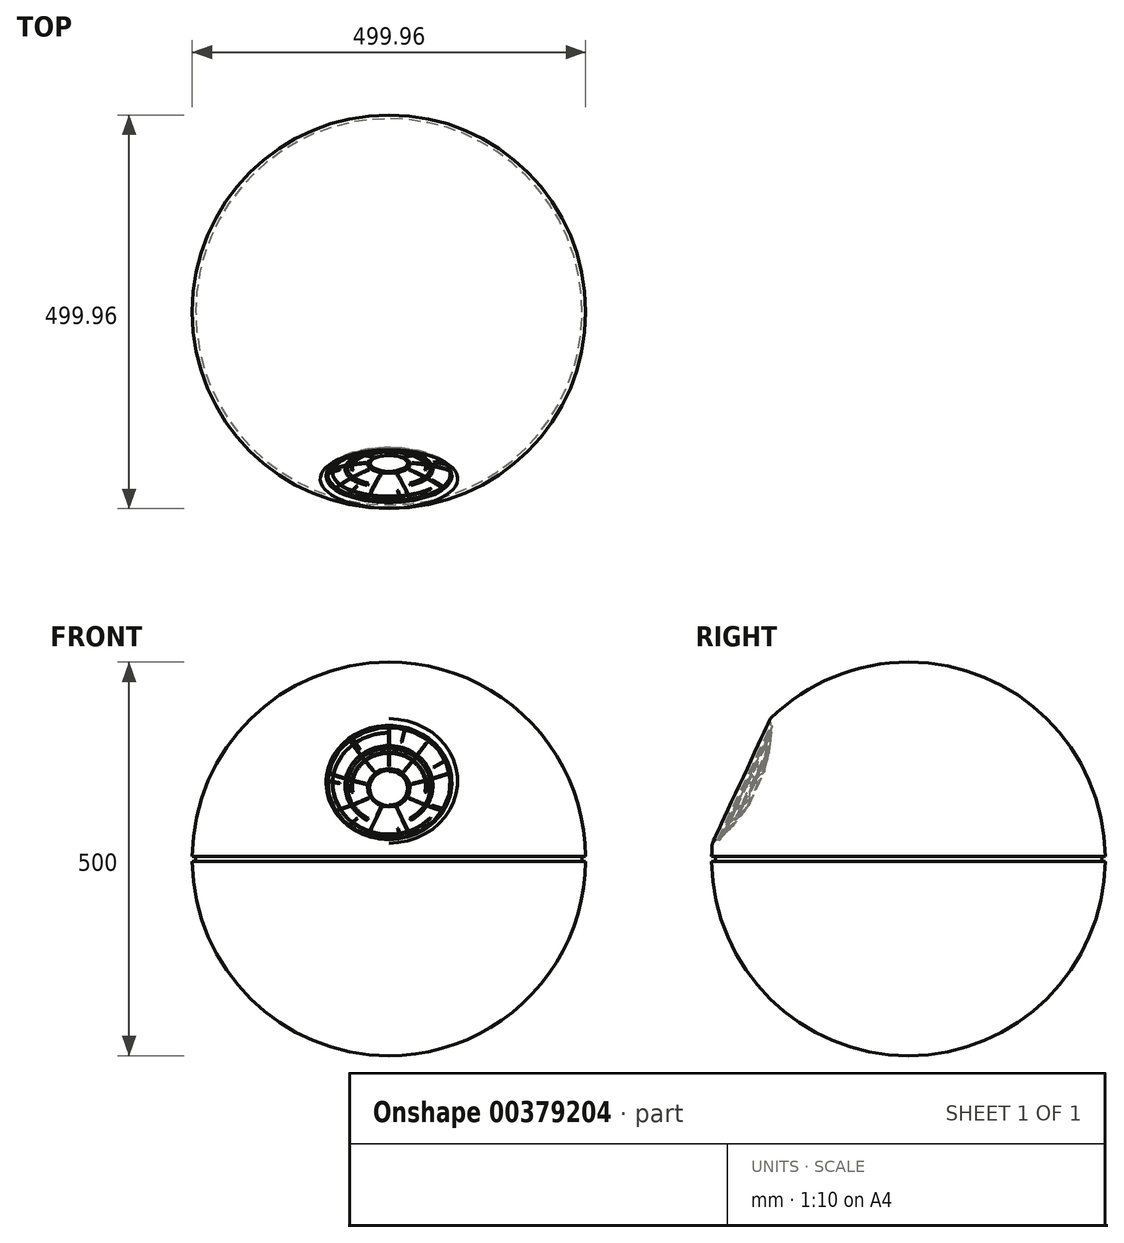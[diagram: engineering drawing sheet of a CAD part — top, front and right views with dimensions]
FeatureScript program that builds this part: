
annotation { "Feature Type Name" : "Feature", "Feature Type Description" : "" }
export const myFeature = defineFeature(function(context is Context, id is Id, definition is map)
    precondition{}
    {
        {
            var Q0;
            Q0=qCreatedBy(makeId("Front.planeOp"),FACE);
            var sketch = newSketch(context, id + "F0", { "sketchPlane" : qUnion([Q0])});
            skArc(sketch, "E0", {"start": v(0, 250) * mm, "mid": v(-250, 0) * mm, "end": v(0, -250) * mm});
            skLineSegment(sketch, "E1", {"start": v(-366.02, 0) * mm, "end": v(388.68, 0) * mm, "construction": true});
            skLineSegment(sketch, "E2", {"start": v(0, 250) * mm, "end": v(0, -250) * mm});
            skSolve(sketch);
        }
        {
            var Q0;
            Q0=makeQuery(id+"F0.imprint","IMPRINT",FACE,{"disambiguationData":[TD([[makeQuery(id+"F0.imprint","IMPRINT",EDGE,{"derivedFrom":sQuery(id+"F0.wireOp",EDGE,"E0")}),1.0]])]});
            var Q1;
            Q1=sQuery(id+"F0.wireOp",EDGE,"E2");
            revolve(context, id + "F1", {"entities" : qUnion([Q0]), "axis" : qUnion([Q1]), "revolveType" : RevolveType.FULL});
        }
        {
            var Q0;
            Q0=qCreatedBy(makeId("Front.planeOp"),FACE);
            var sketch = newSketch(context, id + "F2", { "sketchPlane" : qUnion([Q0])});
            skLineSegment(sketch, "E3.bottom", {"start": v(-261.33, 3) * mm, "end": v(-245.35, 3) * mm});
            skLineSegment(sketch, "E3.top", {"start": v(-261.33, -3) * mm, "end": v(-245.35, -3) * mm});
            skLineSegment(sketch, "E3.left", {"start": v(-261.33, 3) * mm, "end": v(-261.33, -3) * mm});
            skLineSegment(sketch, "E3.right", {"start": v(-245.35, 3) * mm, "end": v(-245.35, -3) * mm});
            skLineSegment(sketch, "E4", {"start": v(-358.16, 0) * mm, "end": v(373.61, 0) * mm, "construction": true});
            skLineSegment(sketch, "E5", {"start": v(0, 342.47) * mm, "end": v(0, -363.32) * mm, "construction": true});
            skSolve(sketch);
        }
        {
            var Q0;
            Q0=makeQuery(id+"F2.imprint","IMPRINT",FACE,{"disambiguationData":[TD([[makeQuery(id+"F2.imprint","IMPRINT",EDGE,{"derivedFrom":sQuery(id+"F2.wireOp",EDGE,"E3.bottom")}),-1.0]])]});
            var Q1;
            Q1=sQuery(id+"F2.wireOp",EDGE,"E5");
            revolve(context, id + "F3", {"operationType" : NewBodyOperationType.REMOVE, "entities" : qUnion([Q0]), "axis" : qUnion([Q1]), "revolveType" : RevolveType.FULL, "oppositeDirection" : true});
        }
        {
            var Q0;
            Q0=qCreatedBy(makeId("Front.planeOp"),FACE);
            cPlane(context, id + "F4", {"entities" : qUnion([Q0]), "cplaneType" : CPlaneType.OFFSET, "offset" : 250 * mm, "width" : 150 * mm, "height" : 150 * mm});
        }
        {
            var Q0;
            Q0=qCreatedBy(makeId("Right.planeOp"),FACE);
            var sketch = newSketch(context, id + "F5", { "sketchPlane" : qUnion([Q0])});
            skLineSegment(sketch, "E6", {"start": v(-402.96, 0) * mm, "end": v(426.81, 0) * mm, "construction": true});
            skLineSegment(sketch, "E7", {"start": v(0, 0) * mm, "end": v(-367.6, 171.42) * mm, "construction": true});
            skLineSegment(sketch, "E8", {"start": v(-174.7, 169.6) * mm, "end": v(-175.43, 178.2) * mm});
            skLineSegment(sketch, "E9", {"start": v(-175.43, 178.2) * mm, "end": v(-202.3, 193.18) * mm});
            skLineSegment(sketch, "E10", {"start": v(-202.3, 193.18) * mm, "end": v(-246.05, 114.73) * mm});
            skLineSegment(sketch, "E11", {"start": v(-246.05, 114.73) * mm, "end": v(-198.64, 92.63) * mm});
            skLineSegment(sketch, "E12", {"start": v(-174.7, 169.6) * mm, "end": v(-172.57, 168.75) * mm});
            skLineSegment(sketch, "E13", {"start": v(-172.57, 168.75) * mm, "end": v(-172.86, 166.94) * mm});
            skLineSegment(sketch, "E14", {"start": v(-172.86, 166.94) * mm, "end": v(-173.77, 166.71) * mm});
            skArc(sketch, "E15", {"start": v(-173.77, 166.71) * mm, "mid": v(-176.2, 140.41) * mm, "end": v(-182.2, 114.7) * mm});
            skLineSegment(sketch, "E16", {"start": v(-182.46, 112.43) * mm, "end": v(-182.2, 114.7) * mm});
            skLineSegment(sketch, "E17", {"start": v(-182.46, 112.43) * mm, "end": v(-182.46, 111.3) * mm});
            skArc(sketch, "E18", {"start": v(-182.46, 111.3) * mm, "mid": v(-191.86, 103.1) * mm, "end": v(-198.64, 92.63) * mm});
            skSolve(sketch);
        }
        {
            var Q0;
            Q0 = qSketchRegion(id + "F5", true);
            var Q1;
            Q1=sQuery(id+"F5.wireOp",EDGE,"E7");
            revolve(context, id + "F6", {"operationType" : NewBodyOperationType.REMOVE, "entities" : qUnion([Q0]), "axis" : qUnion([Q1]), "revolveType" : RevolveType.FULL, "oppositeDirection" : true});
        }
        {
            var Q0;
            Q0=qCreatedBy(makeId("Right.planeOp"),FACE);
            var sketch = newSketch(context, id + "F7", { "sketchPlane" : qUnion([Q0])});
            skFitSpline(sketch, "E19", {"points": [v(-170.94, 164.44) * mm, v(-178.95, 116.7) * mm], "startDerivative": vector(-1.28, -48.1) * mm, "endDerivative": vector(-14.5, -44.6) * mm});
            skLineSegment(sketch, "E20", {"start": v(-170.94, 164.44) * mm, "end": v(-174.49, 164.44) * mm});
            skFitSpline(sketch, "E21", {"points": [v(-174.49, 164.44) * mm, v(-182.1, 117.55) * mm], "startDerivative": vector(-2.02, -46.69) * mm, "endDerivative": vector(-12.28, -42.3) * mm});
            skLineSegment(sketch, "E22", {"start": v(-182.1, 117.55) * mm, "end": v(-178.95, 116.7) * mm});
            skSolve(sketch);
        }
        {
            var Q0;
            Q0 = qSketchRegion(id + "F7", true);
            extrude(context, id + "F8", {"entities" : qUnion([Q0]), "oppositeDirection" : true, "depth" : 1 * mm, "symmetric" : true});
        }
        {
            var Q0;
            Q0=makeQuery(id+"F8.opExtrude","SWEPT_BODY",BODY,{"disambiguationData":[OSD([sQuery(id+"F7.wireOp",EDGE,"E19"),sQuery(id+"F7.wireOp",EDGE,"E20"),sQuery(id+"F7.wireOp",EDGE,"E21"),sQuery(id+"F7.wireOp",EDGE,"E22")])]});
            var Q1;
            Q1=sQuery(id+"F5.wireOp",EDGE,"E7");
            circularPattern(context, id + "F9", {"operationType" : NewBodyOperationType.ADD, "entities" : qUnion([Q0]), "axis" : qUnion([Q1]), "angle" : 360 * degree, "instanceCount" : 9, "equalSpace" : true, "computeTransformsWithoutBuiltin" : true});
        }
        {
            var Q0;
            Q0=qCreatedBy(makeId("Right.planeOp"),FACE);
            var sketch = newSketch(context, id + "F10", { "sketchPlane" : qUnion([Q0])});
            skLineSegment(sketch, "E23", {"start": v(-176.57, 135.51) * mm, "end": v(-178.31, 135.51) * mm});
            skLineSegment(sketch, "E24", {"start": v(-178.31, 135.51) * mm, "end": v(-178.08, 134.16) * mm});
            skLineSegment(sketch, "E25", {"start": v(-176.57, 135.51) * mm, "end": v(-178.08, 134.16) * mm});
            skSolve(sketch);
        }
        {
            var Q0;
            Q0 = qSketchRegion(id + "F10", true);
            var Q1;
            Q1=sQuery(id+"F5.wireOp",EDGE,"E7");
            revolve(context, id + "F11", {"operationType" : NewBodyOperationType.ADD, "entities" : qUnion([Q0]), "axis" : qUnion([Q1]), "revolveType" : RevolveType.SYMMETRIC, "angle" : 200 * degree});
        }
        {
            var Q0;
            Q0=qCreatedBy(makeId("Right.planeOp"),FACE);
            var sketch = newSketch(context, id + "F12", { "sketchPlane" : qUnion([Q0])});
            skLineSegment(sketch, "E26", {"start": v(-172.93, 160.56) * mm, "end": v(-175.44, 160.22) * mm});
            skLineSegment(sketch, "E27", {"start": v(-175.44, 160.22) * mm, "end": v(-172.9, 159.42) * mm});
            skLineSegment(sketch, "E28", {"start": v(-172.9, 159.42) * mm, "end": v(-172.93, 160.56) * mm});
            skSolve(sketch);
        }
        {
            var Q0;
            Q0 = qSketchRegion(id + "F12", true);
            var Q1;
            Q1=sQuery(id+"F5.wireOp",EDGE,"E7");
            revolve(context, id + "F13", {"operationType" : NewBodyOperationType.ADD, "entities" : qUnion([Q0]), "axis" : qUnion([Q1]), "revolveType" : RevolveType.ONE_DIRECTION, "angle" : 227.84 * degree});
        }
        {
            var Q0;
            Q0=qCreatedBy(makeId("Right.planeOp"),FACE);
            var sketch = newSketch(context, id + "F14", { "sketchPlane" : qUnion([Q0])});
            skLineSegment(sketch, "E29", {"start": v(-167.47, 140.14) * mm, "end": v(-176.47, 140.14) * mm});
            skLineSegment(sketch, "E30", {"start": v(-176.47, 140.14) * mm, "end": v(-176.84, 143.97) * mm});
            skLineSegment(sketch, "E31", {"start": v(-167.47, 140.14) * mm, "end": v(-176.84, 143.97) * mm});
            skSolve(sketch);
        }
        {
            var Q0;
            Q0 = qSketchRegion(id + "F14", true);
            var Q1;
            Q1=sQuery(id+"F5.wireOp",EDGE,"E7");
            revolve(context, id + "F15", {"operationType" : NewBodyOperationType.ADD, "entities" : qUnion([Q0]), "axis" : qUnion([Q1]), "revolveType" : RevolveType.SYMMETRIC, "oppositeDirection" : true, "angle" : 300 * degree});
        }
        {
            var Q0;
            Q0=qCreatedBy(makeId("Right.planeOp"),FACE);
            var sketch = newSketch(context, id + "F16", { "sketchPlane" : qUnion([Q0])});
            skFitSpline(sketch, "E32", {"points": [v(-174.06, 165.98) * mm, v(-175.36, 150.25) * mm], "startDerivative": vector(-1.02, -15.25) * mm, "endDerivative": vector(-1.61, -14.66) * mm});
            skLineSegment(sketch, "E33", {"start": v(-174.06, 165.98) * mm, "end": v(-173.3, 165.98) * mm});
            skLineSegment(sketch, "E34", {"start": v(-173.3, 165.98) * mm, "end": v(-174.54, 150.81) * mm});
            skLineSegment(sketch, "E35", {"start": v(-174.54, 150.81) * mm, "end": v(-175.36, 150.25) * mm});
            skSolve(sketch);
        }
        {
            var Q0;
            Q0 = qSketchRegion(id + "F16", true);
            extrude(context, id + "F17", {"entities" : qUnion([Q0]), "depth" : 1 * mm, "symmetric" : true});
        }
        {
            var Q0;
            Q0=makeQuery(id+"F17.opExtrude","SWEPT_BODY",BODY,{"disambiguationData":[OSD([sQuery(id+"F16.wireOp",EDGE,"E32"),sQuery(id+"F16.wireOp",EDGE,"E33"),sQuery(id+"F16.wireOp",EDGE,"E34"),sQuery(id+"F16.wireOp",EDGE,"E35")])]});
            var Q1;
            Q1=sQuery(id+"F5.wireOp",EDGE,"E7");
            transform(context, id + "F18", {"entities" : qUnion([Q0]), "transformType" : TransformType.ROTATION, "transformAxis" : qUnion([Q1]), "angle" : 15 * degree, "oppositeDirection" : true, "makeCopy" : false});
        }
        {
            var Q0;
            Q0=makeQuery(id+"F17.opExtrude","SWEPT_BODY",BODY,{"disambiguationData":[OSD([sQuery(id+"F16.wireOp",EDGE,"E32"),sQuery(id+"F16.wireOp",EDGE,"E33"),sQuery(id+"F16.wireOp",EDGE,"E34"),sQuery(id+"F16.wireOp",EDGE,"E35")])]});
            var Q1;
            Q1=sQuery(id+"F5.wireOp",EDGE,"E7");
            circularPattern(context, id + "F19", {"operationType" : NewBodyOperationType.ADD, "entities" : qUnion([Q0]), "axis" : qUnion([Q1]), "angle" : 360 * degree, "instanceCount" : 7, "equalSpace" : true, "computeTransformsWithoutBuiltin" : true});
        }
    });
